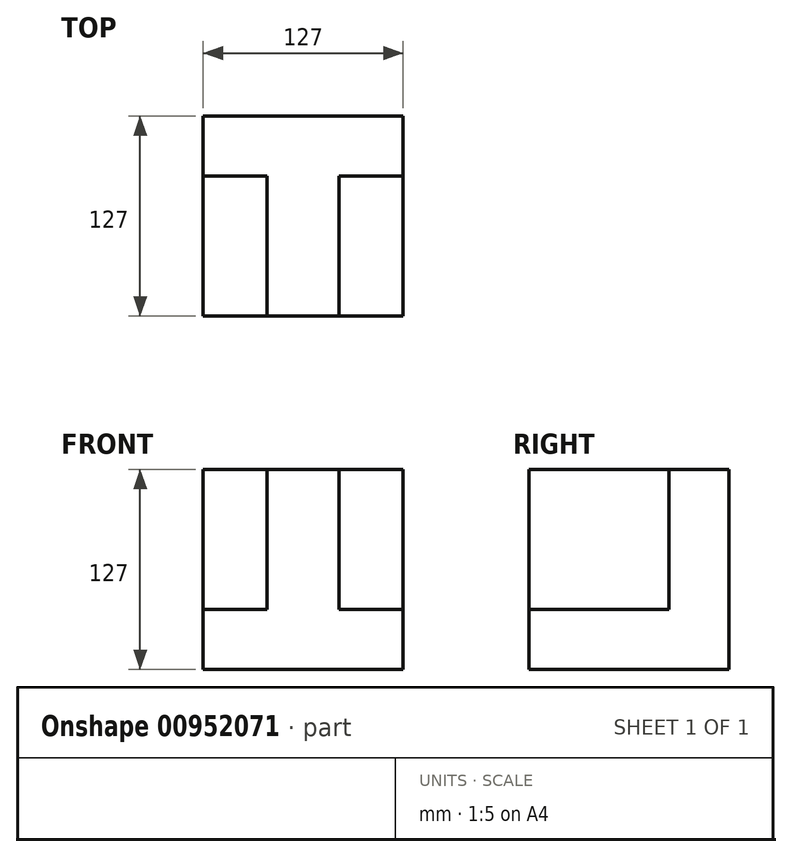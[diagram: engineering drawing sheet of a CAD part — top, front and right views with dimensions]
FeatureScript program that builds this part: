
annotation { "Feature Type Name" : "Feature", "Feature Type Description" : "" }
export const myFeature = defineFeature(function(context is Context, id is Id, definition is map)
    precondition{}
    {
        {
            var Q0;
            Q0=qCreatedBy(makeId("Top.planeOp"),FACE);
            var sketch = newSketch(context, id + "F0", { "sketchPlane" : qUnion([Q0])});
            skLineSegment(sketch, "E0.bottom", {"start": v(-63.5, 63.5) * mm, "end": v(63.5, 63.5) * mm});
            skLineSegment(sketch, "E0.top", {"start": v(-63.5, -63.5) * mm, "end": v(63.5, -63.5) * mm});
            skLineSegment(sketch, "E0.left", {"start": v(-63.5, 63.5) * mm, "end": v(-63.5, -63.5) * mm});
            skLineSegment(sketch, "E0.right", {"start": v(63.5, 63.5) * mm, "end": v(63.5, -63.5) * mm});
            skPoint(sketch, "E0.middle", {"position": v(0, 0) * mm});
            skSolve(sketch);
        }
        {
            var Q0;
            Q0=makeQuery(id+"F0.imprint","IMPRINT",FACE,{"disambiguationData":[TD([[makeQuery(id+"F0.imprint","IMPRINT",EDGE,{"derivedFrom":sQuery(id+"F0.wireOp",EDGE,"E0.bottom")}),-1.0]])]});
            extrude(context, id + "F1", {"entities" : qUnion([Q0]), "depth" : 127 * mm, "offsetDistance" : 25.4 * mm});
        }
        {
            var Q0;
            Q0=makeQuery(id+"F1.opExtrude","CAP_FACE",FACE,{"disambiguationData":[OSD([sQuery(id+"F0.wireOp",EDGE,"E0.bottom"),sQuery(id+"F0.wireOp",EDGE,"E0.top"),sQuery(id+"F0.wireOp",EDGE,"E0.left"),sQuery(id+"F0.wireOp",EDGE,"E0.right")])],"isStart":false});
            var sketch = newSketch(context, id + "F2", { "sketchPlane" : qUnion([Q0])});
            skLineSegment(sketch, "E1.bottom", {"start": v(-63.5, -63.5) * mm, "end": v(-22.86, -63.5) * mm});
            skLineSegment(sketch, "E1.top", {"start": v(-63.5, 25.4) * mm, "end": v(-22.86, 25.4) * mm});
            skLineSegment(sketch, "E1.left", {"start": v(-63.5, -63.5) * mm, "end": v(-63.5, 25.4) * mm});
            skLineSegment(sketch, "E1.right", {"start": v(-22.86, -63.5) * mm, "end": v(-22.86, 25.4) * mm});
            skLineSegment(sketch, "E2.bottom", {"start": v(63.5, -63.5) * mm, "end": v(22.86, -63.5) * mm});
            skLineSegment(sketch, "E2.top", {"start": v(63.5, 25.4) * mm, "end": v(22.86, 25.4) * mm});
            skLineSegment(sketch, "E2.left", {"start": v(63.5, -63.5) * mm, "end": v(63.5, 25.4) * mm});
            skLineSegment(sketch, "E2.right", {"start": v(22.86, -63.5) * mm, "end": v(22.86, 25.4) * mm});
            skSolve(sketch);
        }
        {
            var Q0;
            Q0=makeQuery(id+"F2.imprint","IMPRINT",FACE,{"disambiguationData":[TD([[makeQuery(id+"F2.imprint","IMPRINT",EDGE,{"derivedFrom":sQuery(id+"F2.wireOp",EDGE,"E1.bottom")}),1.0]])]});
            var Q1;
            Q1=makeQuery(id+"F2.imprint","IMPRINT",FACE,{"disambiguationData":[TD([[makeQuery(id+"F2.imprint","IMPRINT",EDGE,{"derivedFrom":sQuery(id+"F2.wireOp",EDGE,"E2.bottom")}),1.0]])]});
            extrude(context, id + "F3", {"entities" : qUnion([Q0, Q1]), "operationType" : NewBodyOperationType.REMOVE, "oppositeDirection" : true, "depth" : 88.9 * mm, "offsetDistance" : 25.4 * mm});
        }
    });
